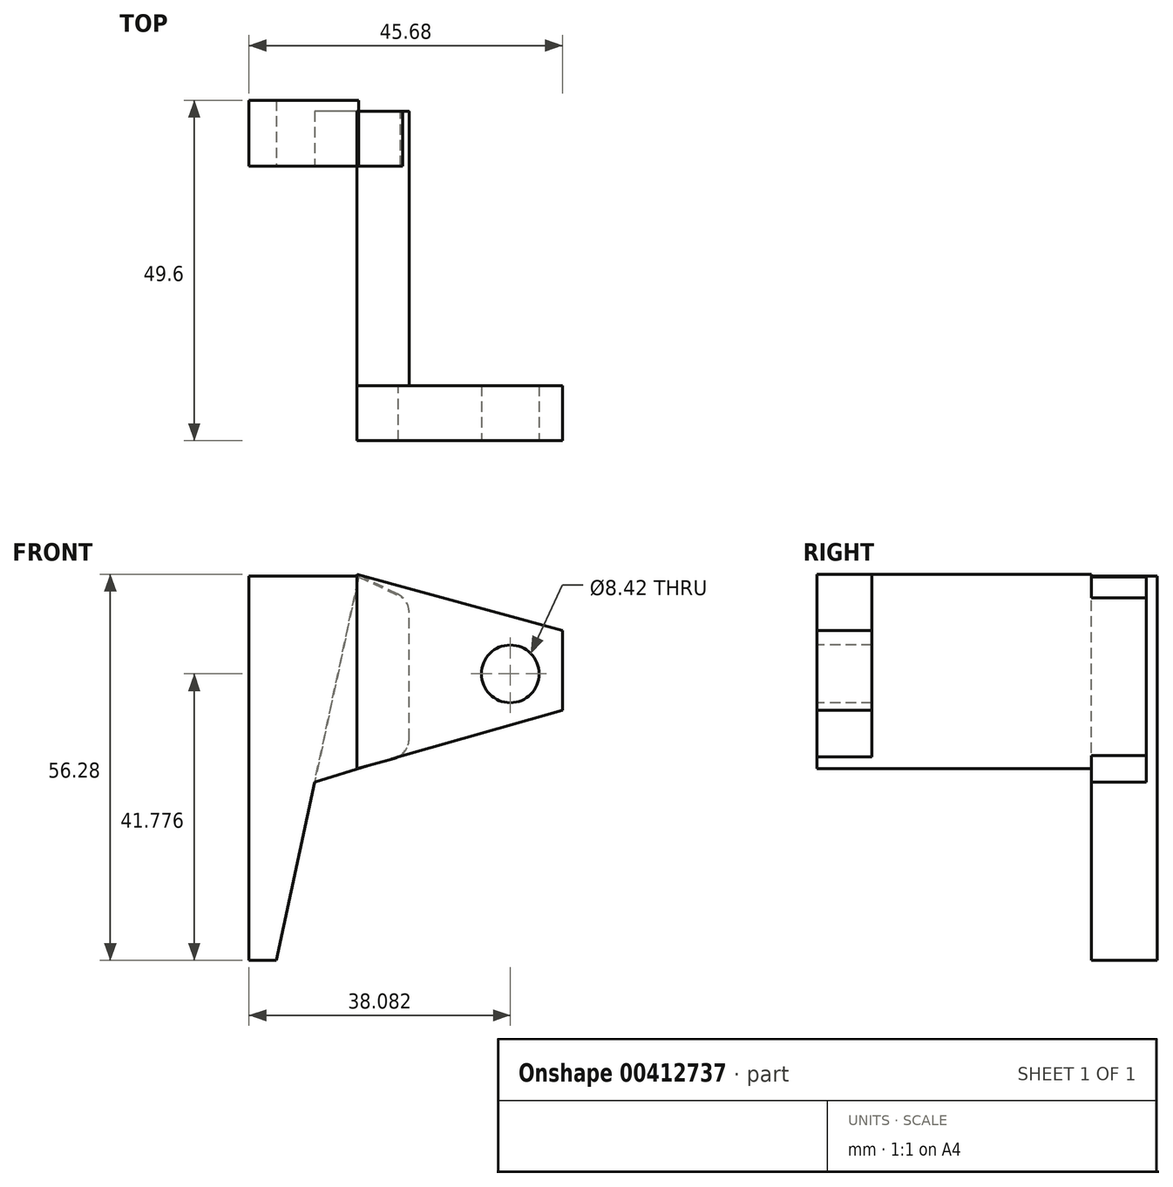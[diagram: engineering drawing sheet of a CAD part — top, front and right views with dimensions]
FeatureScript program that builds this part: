
annotation { "Feature Type Name" : "Feature", "Feature Type Description" : "" }
export const myFeature = defineFeature(function(context is Context, id is Id, definition is map)
    precondition{}
    {
        {
            var Q0;
            Q0=qCreatedBy(makeId("Front.planeOp"),FACE);
            var sketch = newSketch(context, id + "F0", { "sketchPlane" : qUnion([Q0])});
            skLineSegment(sketch, "E0", {"start": v(-35.76, 17.45) * mm, "end": v(-35.76, -38.55) * mm});
            skLineSegment(sketch, "E1", {"start": v(-35.76, -38.55) * mm, "end": v(-31.76, -38.55) * mm});
            skLineSegment(sketch, "E2", {"start": v(-31.76, -38.55) * mm, "end": v(-19.76, 17.45) * mm});
            skLineSegment(sketch, "E3", {"start": v(-19.76, 17.45) * mm, "end": v(-35.76, 17.45) * mm});
            skLineSegment(sketch, "E4", {"start": v(-26.02, -11.74) * mm, "end": v(-19.76, 17.45) * mm});
            skSolve(sketch);
        }
        {
            var Q0;
            Q0=makeQuery(id+"F0.imprint","IMPRINT",FACE,{"disambiguationData":[TD([[makeQuery(id+"F0.imprint","IMPRINT",EDGE,{"derivedFrom":sQuery(id+"F0.wireOp",EDGE,"E0")}),1.0]])]});
            extrude(context, id + "F1", {"entities" : qUnion([Q0]), "oppositeDirection" : true, "depth" : 9.6 * mm});
        }
        {
            var Q0;
            Q0=qCreatedBy(makeId("Front.planeOp"),FACE);
            var sketch = newSketch(context, id + "F2", { "sketchPlane" : qUnion([Q0])});
            skLineSegment(sketch, "E5", {"start": v(-20.03, 17.5) * mm, "end": v(-12.43, 13.89) * mm});
            skLineSegment(sketch, "E6", {"start": v(-12.43, 13.89) * mm, "end": v(-12.43, -8.29) * mm});
            skLineSegment(sketch, "E7", {"start": v(-12.43, -8.29) * mm, "end": v(-26.48, -12.66) * mm});
            skLineSegment(sketch, "E8", {"start": v(-26.48, -12.66) * mm, "end": v(-20.03, 17.5) * mm});
            skSolve(sketch);
        }
        {
            var Q0;
            Q0=makeQuery(id+"F2.imprint","IMPRINT",FACE,{"disambiguationData":[TD([[makeQuery(id+"F2.imprint","IMPRINT",EDGE,{"derivedFrom":sQuery(id+"F2.wireOp",EDGE,"E5")}),-1.0]])]});
            extrude(context, id + "F3", {"entities" : qUnion([Q0]), "operationType" : NewBodyOperationType.ADD, "oppositeDirection" : true, "depth" : 8 * mm});
        }
        {
            var Q0;
            Q0=qCreatedBy(makeId("Front.planeOp"),FACE);
            var sketch = newSketch(context, id + "F4", { "sketchPlane" : qUnion([Q0])});
            skLineSegment(sketch, "E9", {"start": v(-20.03, 17.73) * mm, "end": v(-20.03, -10.6) * mm});
            skLineSegment(sketch, "E10", {"start": v(-20.03, -10.6) * mm, "end": v(-12.43, -8.52) * mm});
            skLineSegment(sketch, "E11", {"start": v(-12.43, -8.52) * mm, "end": v(-12.43, 14.05) * mm});
            skLineSegment(sketch, "E12", {"start": v(-12.43, 14.05) * mm, "end": v(-20.03, 17.73) * mm});
            skSolve(sketch);
        }
        {
            var Q0;
            Q0 = qSketchRegion(id + "F4", true);
            extrude(context, id + "F5", {"entities" : qUnion([Q0]), "operationType" : NewBodyOperationType.ADD, "depth" : 40 * mm});
        }
        {
            var Q0;
            Q0=makeQuery(id+"F5.opExtrude","CAP_FACE",FACE,{"disambiguationData":[OSD([sQuery(id+"F4.wireOp",EDGE,"E9"),sQuery(id+"F4.wireOp",EDGE,"E10"),sQuery(id+"F4.wireOp",EDGE,"E11"),sQuery(id+"F4.wireOp",EDGE,"E12")])],"isStart":false});
            var sketch = newSketch(context, id + "F6", { "sketchPlane" : qUnion([Q0])});
            skLineSegment(sketch, "E13", {"start": v(-20.03, -10.6) * mm, "end": v(17.14, 0) * mm});
            skLineSegment(sketch, "E14", {"start": v(17.14, 0) * mm, "end": v(17.14, 7.55) * mm});
            skLineSegment(sketch, "E15", {"start": v(17.14, 7.55) * mm, "end": v(-20.03, 17.73) * mm});
            skLineSegment(sketch, "E16", {"start": v(-20.03, 17.73) * mm, "end": v(-20.03, -8.52) * mm});
            skSolve(sketch);
        }
        {
            var Q0;
            {var subQ1=sQuery(id+"F6.wireOp",EDGE,"E16");Q0=makeQuery(id+"F6.imprint","IMPRINT",FACE,{"disambiguationData":[TD([[makeQuery(id+"F6.imprint","IMPRINT",EDGE,{"derivedFrom":subQ1}),1.0]])]});}
            var Q1;
            {var subQ1=sQuery(id+"F6.wireOp",EDGE,"E14");Q1=makeQuery(id+"F6.imprint","IMPRINT",FACE,{"disambiguationData":[TD([[makeQuery(id+"F6.imprint","IMPRINT",EDGE,{"derivedFrom":subQ1}),1.0]])]});}
            extrude(context, id + "F7", {"entities" : qUnion([Q0, Q1]), "operationType" : NewBodyOperationType.ADD, "oppositeDirection" : true, "depth" : 8 * mm});
        }
        {
            var Q0;
            {var subQ0=sQuery(id+"F4.wireOp",EDGE,"E9");Q0=makeQuery(id+"F7.boolean.opBoolean","MERGE",FACE,{"derivedFrom":[makeQuery(id+"F5.opExtrude","CAP_FACE",FACE,{"disambiguationData":[OSD([subQ0,sQuery(id+"F4.wireOp",EDGE,"E10"),sQuery(id+"F4.wireOp",EDGE,"E11"),sQuery(id+"F4.wireOp",EDGE,"E12")])],"isStart":false}),makeQuery(id+"F7.opExtrude","CAP_FACE",FACE,{"disambiguationData":[OSD([subQ0,sQuery(id+"F6.wireOp",EDGE,"E13"),sQuery(id+"F6.wireOp",EDGE,"E14"),sQuery(id+"F6.wireOp",EDGE,"E15"),sQuery(id+"F6.wireOp",EDGE,"E16")])],"isStart":true})]});}
            var sketch = newSketch(context, id + "F8", { "sketchPlane" : qUnion([Q0])});
            skCircle(sketch, "E17", {"center": v(2.32, 3.23) * mm, "radius": 4.2 * mm});
            skPoint(sketch, "E17.first.point", {"position": v(4.64, 6.74) * mm});
            skPoint(sketch, "E17.second.point", {"position": v(-1.81, 2.42) * mm});
            skPoint(sketch, "E17.third.point", {"position": v(0, 6.74) * mm});
            skSolve(sketch);
        }
        {
            var Q0;
            Q0=makeQuery(id+"F8.imprint","IMPRINT",FACE,{"disambiguationData":[TD([[makeQuery(id+"F8.imprint","IMPRINT",EDGE,{"derivedFrom":sQuery(id+"F8.wireOp",EDGE,"E17")}),1.0]])]});
            extrude(context, id + "F9", {"entities" : qUnion([Q0]), "operationType" : NewBodyOperationType.REMOVE, "oppositeDirection" : true, "depth" : 8 * mm});
        }
        {
            var Q0;
            {var subQ0=sQuery(id+"F4.wireOp",EDGE,"E9");Q0=makeQuery(id+"F7.boolean.opBoolean","MERGE",FACE,{"derivedFrom":[makeQuery(id+"F5.opExtrude","CAP_FACE",FACE,{"disambiguationData":[OSD([subQ0,sQuery(id+"F4.wireOp",EDGE,"E10"),sQuery(id+"F4.wireOp",EDGE,"E11"),sQuery(id+"F4.wireOp",EDGE,"E12")])],"isStart":false}),makeQuery(id+"F7.opExtrude","CAP_FACE",FACE,{"disambiguationData":[OSD([subQ0,sQuery(id+"F6.wireOp",EDGE,"E13"),sQuery(id+"F6.wireOp",EDGE,"E14"),sQuery(id+"F6.wireOp",EDGE,"E15"),sQuery(id+"F6.wireOp",EDGE,"E16")])],"isStart":true})]});}
            var sketch = newSketch(context, id + "F10", { "sketchPlane" : qUnion([Q0])});
            skLineSegment(sketch, "E18", {"start": v(9.92, 9.53) * mm, "end": v(9.92, -2.06) * mm});
            skLineSegment(sketch, "E19", {"start": v(9.92, -2.06) * mm, "end": v(17.14, 0) * mm});
            skLineSegment(sketch, "E20", {"start": v(17.14, 0) * mm, "end": v(17.14, 7.55) * mm});
            skLineSegment(sketch, "E21", {"start": v(17.14, 7.55) * mm, "end": v(9.92, 9.53) * mm});
            skSolve(sketch);
        }
        {
            var Q0;
            Q0=makeQuery(id+"F10.imprint","IMPRINT",FACE,{"disambiguationData":[TD([[makeQuery(id+"F10.imprint","IMPRINT",EDGE,{"derivedFrom":sQuery(id+"F10.wireOp",EDGE,"E18")}),1.0]])]});
            extrude(context, id + "F11", {"entities" : qUnion([Q0]), "operationType" : NewBodyOperationType.REMOVE, "oppositeDirection" : true, "depth" : 8 * mm});
        }
        {
            var Q0;
            Q0=makeQuery(id+"F11.boolean.opBoolean","COPY",EDGE,{"derivedFrom":makeQuery(id+"F11.opExtrude","SWEPT_EDGE",EDGE,{"disambiguationData":[OSD([sQuery(id+"F6.wireOp",EDGE,"E13"),sQuery(id+"F10.wireOp",EDGE,"E18"),sQuery(id+"F10.wireOp",EDGE,"E19")])]})});
            var Q1;
            Q1=makeQuery(id+"F11.boolean.opBoolean","COPY",EDGE,{"derivedFrom":makeQuery(id+"F11.opExtrude","SWEPT_EDGE",EDGE,{"disambiguationData":[OSD([sQuery(id+"F6.wireOp",EDGE,"E15"),sQuery(id+"F10.wireOp",EDGE,"E18"),sQuery(id+"F10.wireOp",EDGE,"E21")])]})});
            var Q2;
            Q2=makeQuery(id+"F5.opExtrude","SWEPT_EDGE",EDGE,{"disambiguationData":[OSD([sQuery(id+"F4.wireOp",EDGE,"E10"),sQuery(id+"F4.wireOp",EDGE,"E11")])]});
            var Q3;
            Q3=makeQuery(id+"F5.opExtrude","SWEPT_EDGE",EDGE,{"disambiguationData":[OSD([sQuery(id+"F4.wireOp",EDGE,"E11"),sQuery(id+"F4.wireOp",EDGE,"E12")])]});
            fillet(context, id + "F12", {"entities" : qUnion([Q0, Q1, Q2, Q3]), "radius" : 3 * mm, "tangentPropagation" : true, "allowEdgeOverflow" : false});
        }
    });
